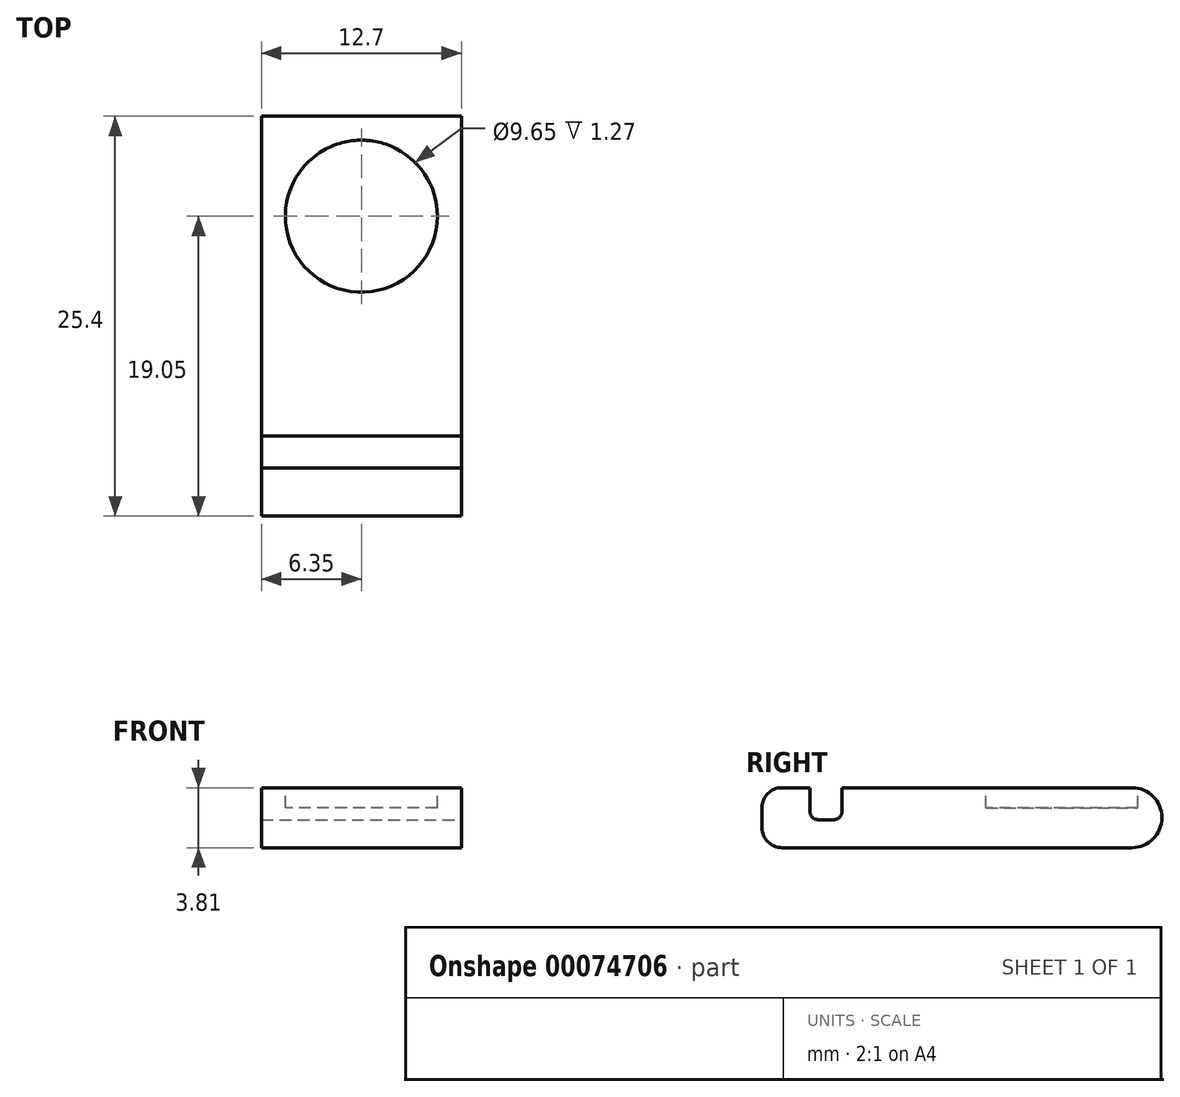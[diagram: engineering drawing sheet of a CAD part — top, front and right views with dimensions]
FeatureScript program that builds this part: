
annotation { "Feature Type Name" : "Feature", "Feature Type Description" : "" }
export const myFeature = defineFeature(function(context is Context, id is Id, definition is map)
    precondition{}
    {
        {
            var Q0;
            Q0=qCreatedBy(makeId("Top.planeOp"),FACE);
            var sketch = newSketch(context, id + "F0", { "sketchPlane" : qUnion([Q0])});
            skLineSegment(sketch, "E0.bottom", {"start": v(0, 0) * mm, "end": v(12.7, 0) * mm});
            skLineSegment(sketch, "E0.top", {"start": v(0, -25.4) * mm, "end": v(12.7, -25.4) * mm});
            skLineSegment(sketch, "E0.left", {"start": v(0, 0) * mm, "end": v(0, -25.4) * mm});
            skLineSegment(sketch, "E0.right", {"start": v(12.7, 0) * mm, "end": v(12.7, -25.4) * mm});
            skSolve(sketch);
        }
        {
            var Q0;
            Q0=makeQuery(id+"F0.imprint","IMPRINT",FACE,{"disambiguationData":[TD([[makeQuery(id+"F0.imprint","IMPRINT",EDGE,{"derivedFrom":sQuery(id+"F0.wireOp",EDGE,"E0.bottom")}),-1.0]])]});
            extrude(context, id + "F1", {"entities" : qUnion([Q0]), "depth" : 3.8 * mm});
        }
        {
            var Q0;
            Q0=makeQuery(id+"F1.opExtrude","CAP_FACE",FACE,{"disambiguationData":[OSD([sQuery(id+"F0.wireOp",EDGE,"E0.bottom"),sQuery(id+"F0.wireOp",EDGE,"E0.top"),sQuery(id+"F0.wireOp",EDGE,"E0.left"),sQuery(id+"F0.wireOp",EDGE,"E0.right")])],"isStart":false});
            var sketch = newSketch(context, id + "F2", { "sketchPlane" : qUnion([Q0])});
            skCircle(sketch, "E1", {"center": v(6.35, -6.35) * mm, "radius": 4.83 * mm});
            skPoint(sketch, "E2.orphan", {"position": v(0, -6.35) * mm});
            skPoint(sketch, "E3.orphan", {"position": v(12.7, -6.35) * mm});
            skSolve(sketch);
        }
        {
            var Q0;
            Q0=makeQuery(id+"F2.imprint","IMPRINT",FACE,{"disambiguationData":[TD([[makeQuery(id+"F2.imprint","IMPRINT",EDGE,{"derivedFrom":sQuery(id+"F2.wireOp",EDGE,"E1")}),1.0]])]});
            extrude(context, id + "F3", {"entities" : qUnion([Q0]), "operationType" : NewBodyOperationType.REMOVE, "oppositeDirection" : true, "depth" : 1.27 * mm});
        }
        {
            var Q0;
            Q0=makeQuery(id+"F1.opExtrude","SWEPT_FACE",FACE,{"disambiguationData":[OSD([sQuery(id+"F0.wireOp",EDGE,"E0.right")])]});
            var sketch = newSketch(context, id + "F4", { "sketchPlane" : qUnion([Q0])});
            skLineSegment(sketch, "E4.bottom", {"start": v(-20.32, 3.81) * mm, "end": v(-22.35, 3.81) * mm});
            skLineSegment(sketch, "E4.top", {"start": v(-20.32, 1.78) * mm, "end": v(-22.35, 1.78) * mm});
            skLineSegment(sketch, "E4.left", {"start": v(-20.32, 3.81) * mm, "end": v(-20.32, 1.78) * mm});
            skLineSegment(sketch, "E4.right", {"start": v(-22.35, 3.81) * mm, "end": v(-22.35, 1.78) * mm});
            skSolve(sketch);
        }
        {
            var Q0;
            Q0=makeQuery(id+"F4.imprint","IMPRINT",FACE,{"disambiguationData":[TD([[makeQuery(id+"F4.imprint","IMPRINT",EDGE,{"derivedFrom":sQuery(id+"F4.wireOp",EDGE,"E4.bottom")}),1.0]])]});
            extrude(context, id + "F5", {"entities" : qUnion([Q0]), "operationType" : NewBodyOperationType.REMOVE, "oppositeDirection" : true, "depth" : 25.4 * mm});
        }
        {
            var Q0;
            Q0=makeQuery(id+"F5.boolean.opBoolean","COPY",EDGE,{"derivedFrom":makeQuery(id+"F5.opExtrude","SWEPT_EDGE",EDGE,{"disambiguationData":[OSD([sQuery(id+"F4.wireOp",EDGE,"E4.top"),sQuery(id+"F4.wireOp",EDGE,"E4.left")])]})});
            var Q1;
            Q1=makeQuery(id+"F5.boolean.opBoolean","COPY",EDGE,{"derivedFrom":makeQuery(id+"F5.opExtrude","SWEPT_EDGE",EDGE,{"disambiguationData":[OSD([sQuery(id+"F4.wireOp",EDGE,"E4.top"),sQuery(id+"F4.wireOp",EDGE,"E4.right")])]})});
            fillet(context, id + "F6", {"entities" : qUnion([Q0, Q1]), "radius" : 0.5 * mm, "tangentPropagation" : true, "allowEdgeOverflow" : false});
        }
        {
            var Q0;
            Q0=makeQuery(id+"F1.opExtrude","CAP_EDGE",EDGE,{"disambiguationData":[OSD([sQuery(id+"F0.wireOp",EDGE,"E0.bottom")])],"isStart":true});
            var Q1;
            Q1=makeQuery(id+"F1.opExtrude","CAP_EDGE",EDGE,{"disambiguationData":[OSD([sQuery(id+"F0.wireOp",EDGE,"E0.bottom")])],"isStart":false});
            fillet(context, id + "F7", {"entities" : qUnion([Q0, Q1]), "radius" : 1.9 * mm, "tangentPropagation" : true, "allowEdgeOverflow" : false});
        }
        {
            var Q0;
            Q0=makeQuery(id+"F1.opExtrude","CAP_EDGE",EDGE,{"disambiguationData":[OSD([sQuery(id+"F0.wireOp",EDGE,"E0.top")])],"isStart":false});
            var Q1;
            Q1=makeQuery(id+"F1.opExtrude","CAP_EDGE",EDGE,{"disambiguationData":[OSD([sQuery(id+"F0.wireOp",EDGE,"E0.top")])],"isStart":true});
            fillet(context, id + "F8", {"entities" : qUnion([Q0, Q1]), "radius" : 1.27 * mm, "tangentPropagation" : true, "allowEdgeOverflow" : false});
        }
    });
